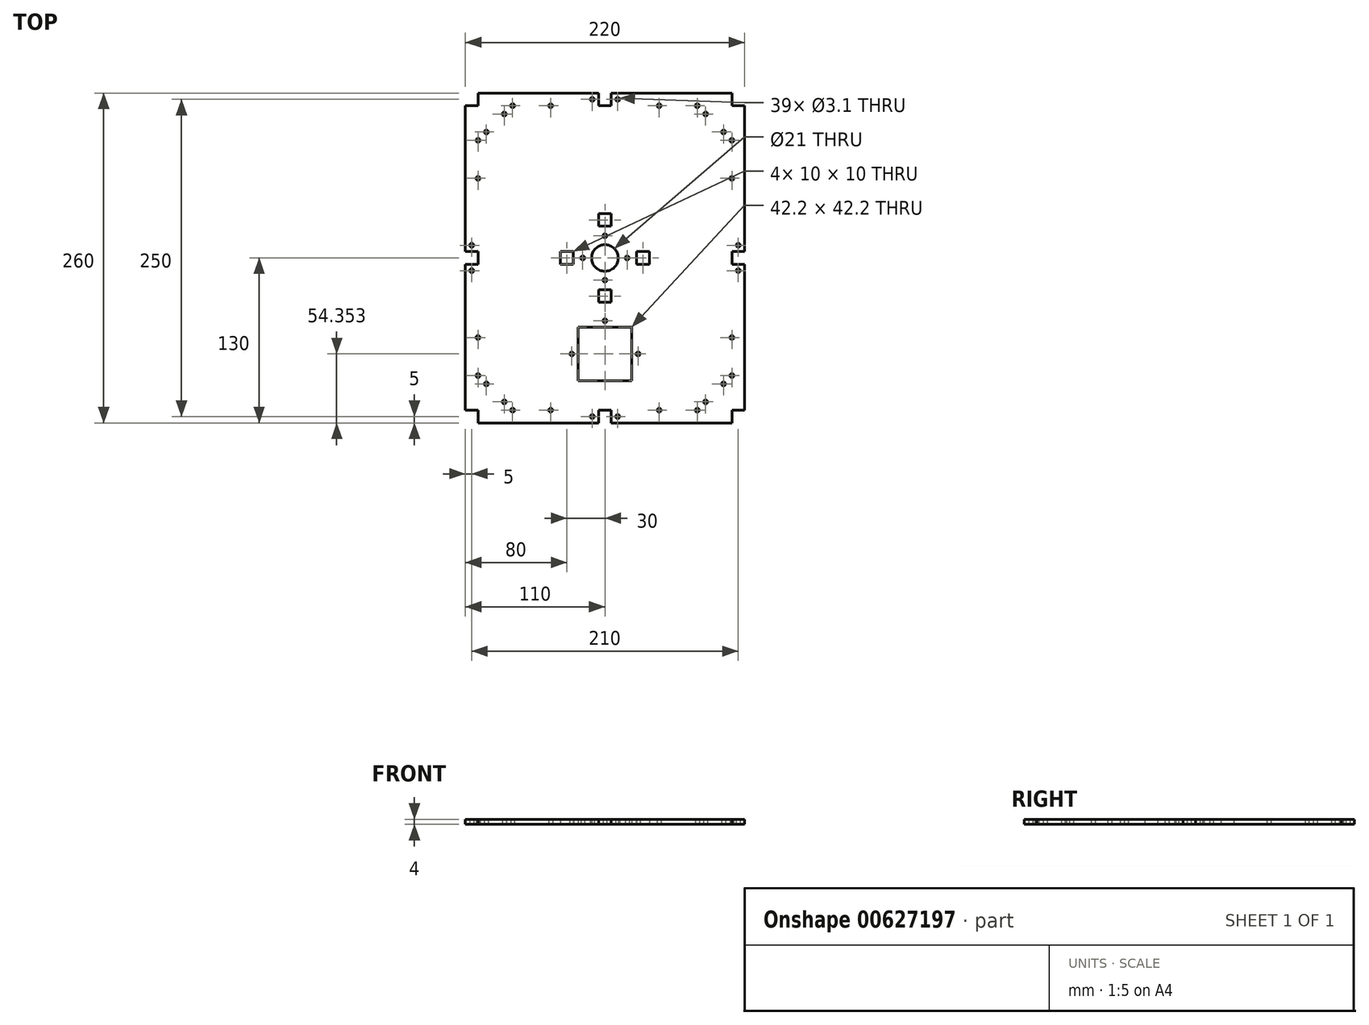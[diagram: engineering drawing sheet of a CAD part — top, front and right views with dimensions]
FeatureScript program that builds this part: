
annotation { "Feature Type Name" : "Feature", "Feature Type Description" : "" }
export const myFeature = defineFeature(function(context is Context, id is Id, definition is map)
    precondition{}
    {
        {
            var Q0;
            Q0=qCreatedBy(makeId("Top.planeOp"),FACE);
            var sketch = newSketch(context, id + "F0", { "sketchPlane" : qUnion([Q0])});
            skLineSegment(sketch, "E0.top", {"start": v(-110, 120) * mm, "end": v(-100, 120) * mm});
            skLineSegment(sketch, "E0.right", {"start": v(-100, 130) * mm, "end": v(-100, 120) * mm});
            skLineSegment(sketch, "E1.top", {"start": v(110, 120) * mm, "end": v(100, 120) * mm});
            skLineSegment(sketch, "E1.right", {"start": v(100, 130) * mm, "end": v(100, 120) * mm});
            skLineSegment(sketch, "E2.top", {"start": v(110, -120) * mm, "end": v(100, -120) * mm});
            skLineSegment(sketch, "E2.right", {"start": v(100, -130) * mm, "end": v(100, -120) * mm});
            skLineSegment(sketch, "E3.top", {"start": v(-110, -120) * mm, "end": v(-100, -120) * mm});
            skLineSegment(sketch, "E3.right", {"start": v(-100, -130) * mm, "end": v(-100, -120) * mm});
            skCircle(sketch, "E4", {"center": v(-100, 92.73) * mm, "radius": 1.55 * mm});
            skCircle(sketch, "E5", {"center": v(-100, 62.73) * mm, "radius": 1.55 * mm});
            skLineSegment(sketch, "E6", {"start": v(-110, 130) * mm, "end": v(-100, 120) * mm, "construction": true});
            skCircle(sketch, "E7.MirrorC", {"center": v(-72.73, 120) * mm, "radius": 1.55 * mm});
            skCircle(sketch, "E8.MirrorC", {"center": v(-42.73, 120) * mm, "radius": 1.55 * mm});
            skLineSegment(sketch, "E9", {"start": v(0, 199.29) * mm, "end": v(0, -220.71) * mm, "construction": true});
            skLineSegment(sketch, "E10", {"start": v(-220.2, 0) * mm, "end": v(179.8, 0) * mm, "construction": true});
            skLineSegment(sketch, "E11", {"start": v(55, 199.29) * mm, "end": v(55, -220.71) * mm, "construction": true});
            skLineSegment(sketch, "E12", {"start": v(-55, 199.29) * mm, "end": v(-55, -220.71) * mm, "construction": true});
            skCircle(sketch, "E13.MirrorC", {"center": v(42.73, 120) * mm, "radius": 1.55 * mm});
            skCircle(sketch, "E14.MirrorC", {"center": v(72.73, 120) * mm, "radius": 1.55 * mm});
            skCircle(sketch, "E15.MirrorC", {"center": v(100, 92.73) * mm, "radius": 1.55 * mm});
            skCircle(sketch, "E16.MirrorC", {"center": v(100, 62.73) * mm, "radius": 1.55 * mm});
            skCircle(sketch, "E17.MirrorC", {"center": v(-100, -62.74) * mm, "radius": 1.55 * mm});
            skCircle(sketch, "E18.MirrorC", {"center": v(-100, -92.74) * mm, "radius": 1.55 * mm});
            skCircle(sketch, "E19.MirrorC", {"center": v(-72.73, -120) * mm, "radius": 1.55 * mm});
            skCircle(sketch, "E20.MirrorC", {"center": v(-42.73, -120) * mm, "radius": 1.55 * mm});
            skCircle(sketch, "E21.MirrorC", {"center": v(42.73, -120) * mm, "radius": 1.55 * mm});
            skCircle(sketch, "E22.MirrorC", {"center": v(72.73, -120) * mm, "radius": 1.55 * mm});
            skCircle(sketch, "E23.MirrorC", {"center": v(100, -92.74) * mm, "radius": 1.55 * mm});
            skCircle(sketch, "E24.MirrorC", {"center": v(100, -62.74) * mm, "radius": 1.55 * mm});
            skLineSegment(sketch, "E25.bottom", {"start": v(-110, 5) * mm, "end": v(-100, 5) * mm});
            skLineSegment(sketch, "E25.top", {"start": v(-110, -5) * mm, "end": v(-100, -5) * mm});
            skLineSegment(sketch, "E25.right", {"start": v(-100, 5) * mm, "end": v(-100, -5) * mm});
            skLineSegment(sketch, "E26.MirrorCS", {"start": v(110, 5) * mm, "end": v(100, 5) * mm});
            skLineSegment(sketch, "E27.MirrorCS", {"start": v(110, -5) * mm, "end": v(100, -5) * mm});
            skLineSegment(sketch, "E28.MirrorCS", {"start": v(100, 5) * mm, "end": v(100, -5) * mm});
            skLineSegment(sketch, "E29.bottom", {"start": v(21.1, -96.75) * mm, "end": v(-21.1, -96.75) * mm});
            skLineSegment(sketch, "E29.top", {"start": v(21.1, -54.55) * mm, "end": v(-21.1, -54.55) * mm});
            skLineSegment(sketch, "E29.left", {"start": v(21.1, -96.75) * mm, "end": v(21.1, -54.55) * mm});
            skLineSegment(sketch, "E29.right", {"start": v(-21.1, -96.75) * mm, "end": v(-21.1, -54.55) * mm});
            skPoint(sketch, "E29.middle", {"position": v(0, -75.65) * mm});
            skCircle(sketch, "E30", {"center": v(26.1, -75.65) * mm, "radius": 1.55 * mm});
            skCircle(sketch, "E31", {"center": v(0, -49.55) * mm, "radius": 1.55 * mm});
            skCircle(sketch, "E32.MirrorC", {"center": v(-26.1, -75.65) * mm, "radius": 1.55 * mm});
            skLineSegment(sketch, "E33.bottom", {"start": v(5, 120) * mm, "end": v(-5, 120) * mm});
            skLineSegment(sketch, "E33.left", {"start": v(5, 120) * mm, "end": v(5, 130) * mm});
            skLineSegment(sketch, "E33.right", {"start": v(-5, 120) * mm, "end": v(-5, 130) * mm});
            skPoint(sketch, "E33.middle", {"position": v(0, 125) * mm});
            skLineSegment(sketch, "E34.MirrorCS", {"start": v(-5, -120) * mm, "end": v(-5, -130) * mm});
            skLineSegment(sketch, "E35.MirrorCS", {"start": v(5, -120) * mm, "end": v(5, -130) * mm});
            skLineSegment(sketch, "E36.MirrorCS", {"start": v(5, -120) * mm, "end": v(-5, -120) * mm});
            skCircle(sketch, "E37", {"center": v(10, 125) * mm, "radius": 1.55 * mm});
            skPoint(sketch, "E37.centerSnap0", {"position": v(5, 125) * mm});
            skPoint(sketch, "E37.perimeterSnap0", {"position": v(5, 125) * mm});
            skCircle(sketch, "E38", {"center": v(105, -10) * mm, "radius": 1.55 * mm});
            skPoint(sketch, "E38.centerSnap0", {"position": v(105, -5) * mm});
            skPoint(sketch, "E38.perimeterSnap0", {"position": v(105, -5) * mm});
            skCircle(sketch, "E39", {"center": v(-10, -125) * mm, "radius": 1.55 * mm});
            skPoint(sketch, "E39.centerSnap0", {"position": v(-5, -125) * mm});
            skCircle(sketch, "E40", {"center": v(-105, 10) * mm, "radius": 1.55 * mm});
            skPoint(sketch, "E40.centerSnap0", {"position": v(-105, 5) * mm});
            skCircle(sketch, "E41", {"center": v(0, 0) * mm, "radius": 10.5 * mm});
            skCircle(sketch, "E42", {"center": v(17.5, 0) * mm, "radius": 1.55 * mm});
            skCircle(sketch, "E43", {"center": v(-17.5, 0) * mm, "radius": 1.55 * mm});
            skCircle(sketch, "E44", {"center": v(0, 17.5) * mm, "radius": 1.55 * mm});
            skCircle(sketch, "E45", {"center": v(0, -17.5) * mm, "radius": 1.55 * mm});
            skLineSegment(sketch, "E46.bottom", {"start": v(5, 25) * mm, "end": v(-5, 25) * mm});
            skLineSegment(sketch, "E46.top", {"start": v(5, 35) * mm, "end": v(-5, 35) * mm});
            skLineSegment(sketch, "E46.left", {"start": v(5, 25) * mm, "end": v(5, 35) * mm});
            skLineSegment(sketch, "E46.right", {"start": v(-5, 25) * mm, "end": v(-5, 35) * mm});
            skPoint(sketch, "E46.middle", {"position": v(0, 30) * mm});
            skLineSegment(sketch, "E47.bottom", {"start": v(35, -5) * mm, "end": v(25, -5) * mm});
            skLineSegment(sketch, "E47.top", {"start": v(35, 5) * mm, "end": v(25, 5) * mm});
            skLineSegment(sketch, "E47.left", {"start": v(35, -5) * mm, "end": v(35, 5) * mm});
            skLineSegment(sketch, "E47.right", {"start": v(25, -5) * mm, "end": v(25, 5) * mm});
            skPoint(sketch, "E47.middle", {"position": v(30, 0) * mm});
            skLineSegment(sketch, "E48.bottom", {"start": v(-35, 5) * mm, "end": v(-25, 5) * mm});
            skLineSegment(sketch, "E48.top", {"start": v(-35, -5) * mm, "end": v(-25, -5) * mm});
            skLineSegment(sketch, "E48.left", {"start": v(-35, 5) * mm, "end": v(-35, -5) * mm});
            skLineSegment(sketch, "E48.right", {"start": v(-25, 5) * mm, "end": v(-25, -5) * mm});
            skPoint(sketch, "E48.middle", {"position": v(-30, 0) * mm});
            skLineSegment(sketch, "E49.bottom", {"start": v(5, -35) * mm, "end": v(-5, -35) * mm});
            skLineSegment(sketch, "E49.top", {"start": v(5, -25) * mm, "end": v(-5, -25) * mm});
            skLineSegment(sketch, "E49.left", {"start": v(5, -35) * mm, "end": v(5, -25) * mm});
            skLineSegment(sketch, "E49.right", {"start": v(-5, -35) * mm, "end": v(-5, -25) * mm});
            skPoint(sketch, "E49.middle", {"position": v(0, -30) * mm});
            skLineSegment(sketch, "E50", {"start": v(-100, 92.73) * mm, "end": v(-72.73, 120) * mm, "construction": true});
            skCircle(sketch, "E51", {"center": v(-93.44, 99.3) * mm, "radius": 1.55 * mm});
            skCircle(sketch, "E52", {"center": v(-79.3, 113.44) * mm, "radius": 1.55 * mm});
            skLineSegment(sketch, "E53.MirrorCS", {"start": v(-100, -92.74) * mm, "end": v(-72.73, -120) * mm, "construction": true});
            skCircle(sketch, "E54.MirrorC", {"center": v(93.44, 99.3) * mm, "radius": 1.55 * mm});
            skLineSegment(sketch, "E55.MirrorCS", {"start": v(100, 92.73) * mm, "end": v(72.73, 120) * mm, "construction": true});
            skCircle(sketch, "E56.MirrorC", {"center": v(79.3, 113.44) * mm, "radius": 1.55 * mm});
            skCircle(sketch, "E57.MirrorC", {"center": v(93.44, -99.3) * mm, "radius": 1.55 * mm});
            skLineSegment(sketch, "E58.MirrorCS", {"start": v(100, -92.74) * mm, "end": v(72.73, -120) * mm, "construction": true});
            skCircle(sketch, "E59.MirrorC", {"center": v(79.3, -113.44) * mm, "radius": 1.55 * mm});
            skCircle(sketch, "E60.MirrorC", {"center": v(-93.44, -99.3) * mm, "radius": 1.55 * mm});
            skCircle(sketch, "E61.MirrorC", {"center": v(-79.3, -113.44) * mm, "radius": 1.55 * mm});
            skCircle(sketch, "E62.MirrorC", {"center": v(105, 10) * mm, "radius": 1.55 * mm});
            skCircle(sketch, "E63.MirrorC", {"center": v(-105, -10) * mm, "radius": 1.55 * mm});
            skCircle(sketch, "E64.MirrorC", {"center": v(10, -125) * mm, "radius": 1.55 * mm});
            skCircle(sketch, "E65.MirrorC", {"center": v(-10, 125) * mm, "radius": 1.55 * mm});
            skLineSegment(sketch, "E66", {"start": v(-100, -130) * mm, "end": v(-5, -130) * mm});
            skLineSegment(sketch, "E67", {"start": v(5, -130) * mm, "end": v(100, -130) * mm});
            skLineSegment(sketch, "E68", {"start": v(-110, -120) * mm, "end": v(-110, -5) * mm});
            skLineSegment(sketch, "E69", {"start": v(-110, 5) * mm, "end": v(-110, 120) * mm});
            skLineSegment(sketch, "E70", {"start": v(-100, 130) * mm, "end": v(-5, 130) * mm});
            skLineSegment(sketch, "E71", {"start": v(100, 130) * mm, "end": v(5, 130) * mm});
            skLineSegment(sketch, "E72", {"start": v(110, 120) * mm, "end": v(110, 5) * mm});
            skLineSegment(sketch, "E73", {"start": v(110, -5) * mm, "end": v(110, -120) * mm});
            skSolve(sketch);
        }
        {
            var Q0;
            {var subQ4=sQuery(id+"F0.wireOp",EDGE,"E0.top");Q0=makeQuery(id+"F0.imprint","IMPRINT",FACE,{"disambiguationData":[TD([[makeQuery(id+"F0.imprint","IMPRINT",EDGE,{"derivedFrom":subQ4}),-1.0]])]});}
            extrude(context, id + "F1", {"entities" : qUnion([Q0]), "depth" : 4 * mm, "offsetDistance" : 25 * mm});
        }
    });
